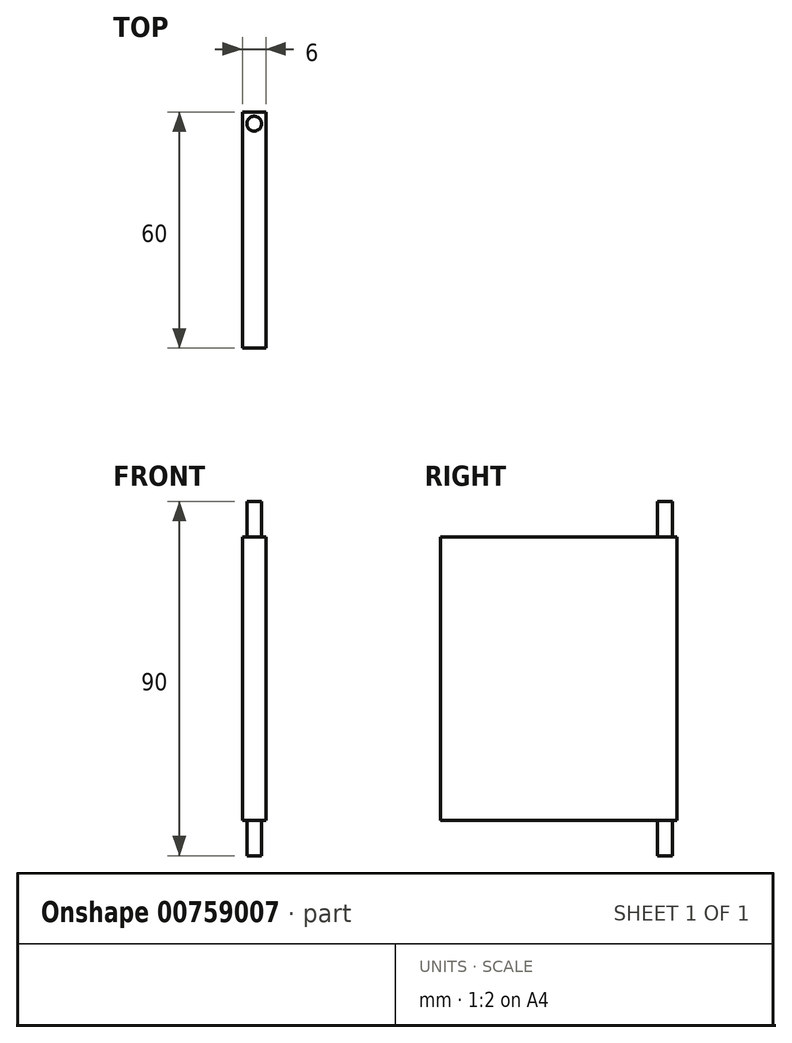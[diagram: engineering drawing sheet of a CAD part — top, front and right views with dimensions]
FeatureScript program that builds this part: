
annotation { "Feature Type Name" : "Feature", "Feature Type Description" : "" }
export const myFeature = defineFeature(function(context is Context, id is Id, definition is map)
    precondition{}
    {
        {
            var Q0;
            Q0=qCreatedBy(makeId("Top.planeOp"),FACE);
            var sketch = newSketch(context, id + "F0", { "sketchPlane" : qUnion([Q0])});
            skLineSegment(sketch, "E0.bottom", {"start": v(-3, 30) * mm, "end": v(3, 30) * mm});
            skLineSegment(sketch, "E0.top", {"start": v(-3, -30) * mm, "end": v(3, -30) * mm});
            skLineSegment(sketch, "E0.left", {"start": v(-3, 30) * mm, "end": v(-3, -30) * mm});
            skLineSegment(sketch, "E0.right", {"start": v(3, 30) * mm, "end": v(3, -30) * mm});
            skPoint(sketch, "E0.middle", {"position": v(0, 0) * mm});
            skSolve(sketch);
        }
        {
            var Q0;
            Q0=makeQuery(id+"F0.imprint","IMPRINT",FACE,{"disambiguationData":[TD([[makeQuery(id+"F0.imprint","IMPRINT",EDGE,{"derivedFrom":sQuery(id+"F0.wireOp",EDGE,"E0.bottom")}),-1.0]])]});
            extrude(context, id + "F1", {"entities" : qUnion([Q0]), "depth" : 90 * mm, "offsetDistance" : 25 * mm});
        }
        {
            var Q0;
            Q0=makeQuery(id+"F1.opExtrude","CAP_FACE",FACE,{"disambiguationData":[OSD([sQuery(id+"F0.wireOp",EDGE,"E0.bottom"),sQuery(id+"F0.wireOp",EDGE,"E0.top"),sQuery(id+"F0.wireOp",EDGE,"E0.left"),sQuery(id+"F0.wireOp",EDGE,"E0.right")])],"isStart":false});
            var sketch = newSketch(context, id + "F2", { "sketchPlane" : qUnion([Q0])});
            skCircle(sketch, "E1", {"center": v(0, -27) * mm, "radius": 1.88 * mm});
            skCircle(sketch, "E2.MirrorC", {"center": v(0, 27) * mm, "radius": 1.88 * mm});
            skSolve(sketch);
        }
        {
            var Q0;
            Q0=makeQuery(id+"F2.imprint","IMPRINT",FACE,{"disambiguationData":[TD([[makeQuery(id+"F2.imprint","IMPRINT",EDGE,{"derivedFrom":sQuery(id+"F2.wireOp",EDGE,"E2.MirrorC")}),-1.0]])]});
            var Q1;
            Q1=makeQuery(id+"F2.imprint","IMPRINT",FACE,{"disambiguationData":[TD([[makeQuery(id+"F2.imprint","IMPRINT",EDGE,{"derivedFrom":sQuery(id+"F2.wireOp",EDGE,"E1")}),1.0]])]});
            extrude(context, id + "F3", {"entities" : qUnion([Q0, Q1]), "operationType" : NewBodyOperationType.REMOVE, "oppositeDirection" : true, "depth" : 9 * mm, "offsetDistance" : 25 * mm});
        }
        {
            var Q0;
            Q0=makeQuery(id+"F1.opExtrude","CAP_FACE",FACE,{"disambiguationData":[OSD([sQuery(id+"F0.wireOp",EDGE,"E0.bottom"),sQuery(id+"F0.wireOp",EDGE,"E0.top"),sQuery(id+"F0.wireOp",EDGE,"E0.left"),sQuery(id+"F0.wireOp",EDGE,"E0.right")])],"isStart":true});
            var sketch = newSketch(context, id + "F4", { "sketchPlane" : qUnion([Q0])});
            skCircle(sketch, "E3", {"center": v(0, 27) * mm, "radius": 1.88 * mm});
            skCircle(sketch, "E4.MirrorC", {"center": v(0, -27) * mm, "radius": 1.88 * mm});
            skSolve(sketch);
        }
        {
            var Q0;
            Q0=makeQuery(id+"F4.imprint","IMPRINT",FACE,{"disambiguationData":[TD([[makeQuery(id+"F4.imprint","IMPRINT",EDGE,{"derivedFrom":sQuery(id+"F4.wireOp",EDGE,"E3")}),1.0]])]});
            var Q1;
            Q1=makeQuery(id+"F4.imprint","IMPRINT",FACE,{"disambiguationData":[TD([[makeQuery(id+"F4.imprint","IMPRINT",EDGE,{"derivedFrom":sQuery(id+"F4.wireOp",EDGE,"E4.MirrorC")}),-1.0]])]});
            extrude(context, id + "F5", {"entities" : qUnion([Q0, Q1]), "operationType" : NewBodyOperationType.REMOVE, "oppositeDirection" : true, "depth" : 9 * mm, "offsetDistance" : 25 * mm});
        }
    });
